# Revit family: Toilet-Wall_Mount-KOHLER-Patio-K-18131IN
name_source: partatom
category: Plumbing Fixtures
revit_build: Autodesk Revit 2017 (Build: 20160225_1515(x64)
units: mm (PartAtom-declared; Revit-internal decimal feet)

## family parameters
Cut with Voids When Loaded = No
Host = Face
OmniClass Number = 23.31.19.00
OmniClass Title = Toilets
Part Type = Normal
Room Calculation Point = No
Round Connector Dimension = Use Diameter
Shared = No

## types (3) — shared parameters
ADA Compliant = No
Assembly Code = D2010100
CW Connection = Yes
Cold Water Inlet = Cold Water Inlet
Date Modified = 01/11/2021
Default Elevation = 0"
Description = Wall-Hung Toilet With Quiet-Close™ Seat and Cover
Flow Rate = 0 GPM
Flush Rate- GPF = 0 GPF
Flush Rate- LPF = 0 LPF
HW Connection = No
Height = 16 9/16"
Hot Water Inlet = Hot Water Inlet
Length = 21 1/2"
Manufacturer = KOHLER Co.
Master Format 2014 = 22 42 13.13
Master Format 2014 Name = Residential Water Closets
Material = Vitreous China
Pressure = 0.00 psi
Product Documentation Link = http://resources.kohler.com
Product Name = Patio
Product Page URL = https://www.kohler.co.in
Seat Included = Yes
URL = https://www.kohler.co.in
Vent Connection = No
Waste Connection = Yes
Waste Water Outlet = Waste Water Outlet
WaterSense Certified = No
Width = 14 11/16"

## per-type parameters (varying)
| type | Finish | Model | Type |
| 0-White | Kohler-Vitreous_China-0-White | K-18131IN-S-0 | 1 |
| 96-Biscuit | Kohler-Vitreous_China-96-Biscuit | K-18131IN-S-96 | 2 |
| 7-Black Black | Kohler-Plastic-7-Black_Black | K-18131IN-S-7 | 3 |

## geometry (parser evidence)
native form markers: Sweep x6
no freeform markers — native parametric forms only
